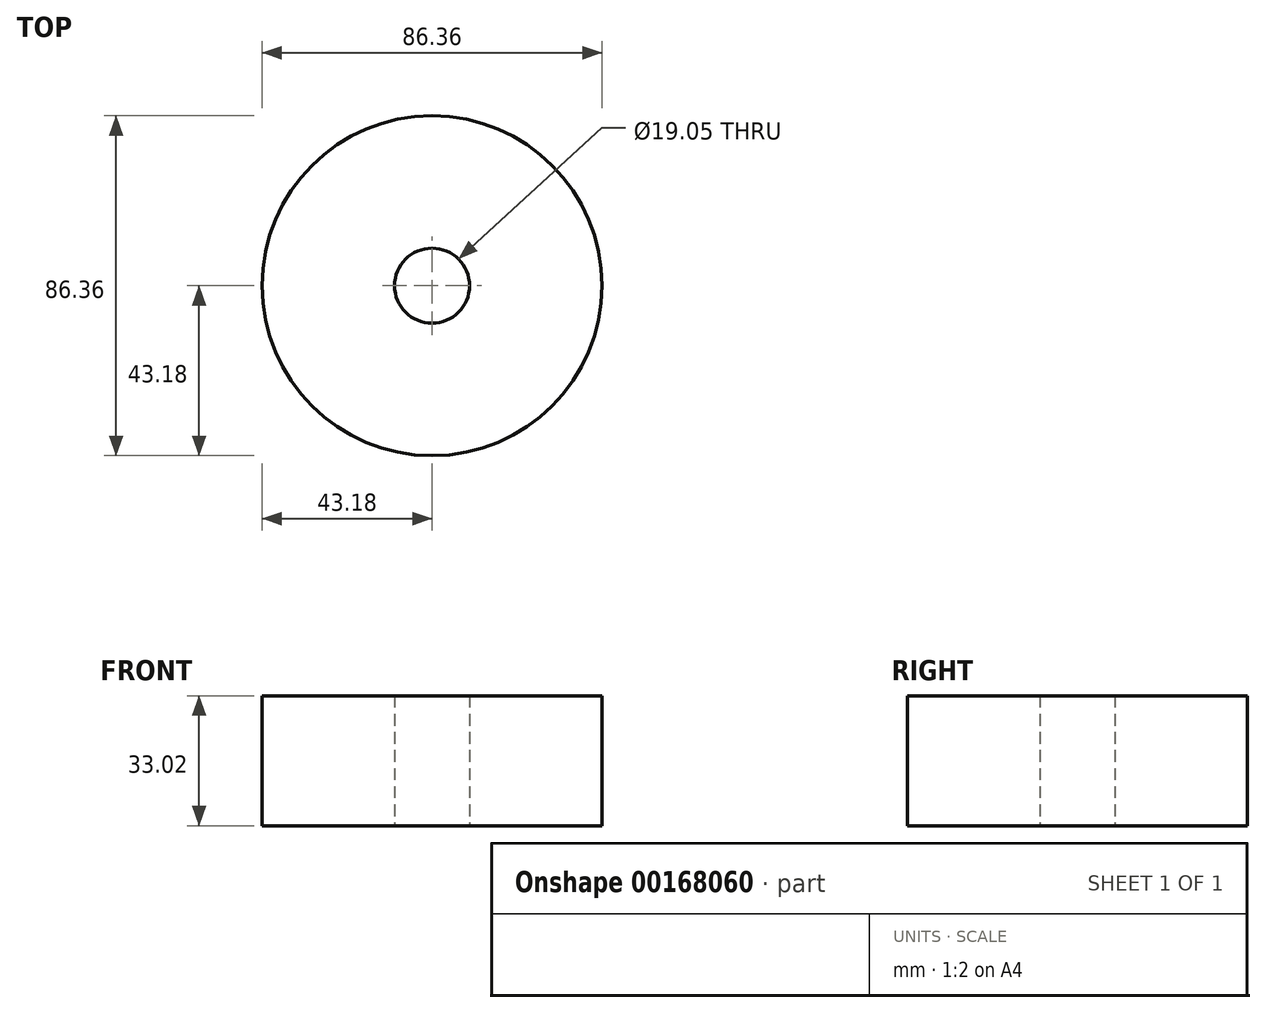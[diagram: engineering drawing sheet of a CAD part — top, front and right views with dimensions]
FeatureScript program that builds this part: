
annotation { "Feature Type Name" : "Feature", "Feature Type Description" : "" }
export const myFeature = defineFeature(function(context is Context, id is Id, definition is map)
    precondition{}
    {
        {
            var Q0;
            Q0=qCreatedBy(makeId("Top.planeOp"),FACE);
            var sketch = newSketch(context, id + "F0", { "sketchPlane" : qUnion([Q0])});
            skCircle(sketch, "E0", {"center": v(0, 0) * mm, "radius": 43.18 * mm});
            skCircle(sketch, "E1", {"center": v(0, 0) * mm, "radius": 9.53 * mm});
            skSolve(sketch);
        }
        {
            var Q0;
            Q0=qSketchRegion(id+"F0",true);
            extrude(context, id + "F1", {"entities" : qUnion([Q0]), "depth" : 33.02 * mm});
        }
    });
